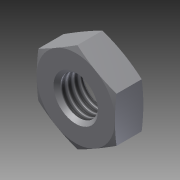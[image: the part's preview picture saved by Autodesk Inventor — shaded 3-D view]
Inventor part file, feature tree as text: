
AUTODESK INVENTOR PART (.ipt)
format: ipt  version: 2012 (Build 160160000, 160)  size: 142,848 bytes
history: native  units: in
note: dims shown in document units (in); Inventor stores cm internally (conversion verified against a paired STEP export)
features: other x70, sketch x3, revolve x2, extrude x1, thread x1
ambient origin geometry x8: Origin, YZ Plane, XZ Plane, XY Plane, X Axis, Y Axis, Z Axis, Center Point
bodies: Solid1 (feature_tree)
feature tree (77):
  sketch  "Sketch_8"  dims[d0=360.0deg d1=0.16in d2=0.0in]
  sketch  "Sketch_10"  dims[d3=360.0deg d4=0.1213in d5=0.0in]
  revolve  "Revolution1"  [1 undecoded]
  extrude  "Extrusion1"  Depth=0.1213in TaperAngle=0.0deg
  revolve  "Revolution2"  [1 undecoded]
  thread  "Thread1"  [1 undecoded]
  other  "NUT_XY"
  other  "NUT_YZ"
  other  "NUT_ZX"
  other  "NUT_X"
  other  "NUT_Y"
  other  "NUT_Z"
  other  "NUT_Center"
  other  "a1_XY"
  other  "a1_YZ"
  other  "a1_ZX"
  other  "a1_X"
  other  "a1_Y"
  other  "a1_Z"
  other  "a1_Center"
  other  "a2_XY"
  other  "a2_YZ"
  other  "a2_ZX"
  other  "a2_X"
  other  "a2_Y"
  other  "a2_Z"
  other  "a2_Center"
  other  "b1_XY"
  other  "b1_YZ"
  other  "b1_ZX"
  other  "b1_X"
  other  "b1_Y"
  other  "b1_Z"
  other  "b1_Center"
  other  "b2_XY"
  other  "b2_YZ"
  other  "b2_ZX"
  other  "b2_X"
  other  "b2_Y"
  other  "b2_Z"
  other  "b2_Center"
  other  "e_XY"
  other  "e_YZ"
  other  "e_ZX"
  other  "e_X"
  other  "e_Y"
  other  "e_Z"
  other  "e_Center"
  other  "th1_XY"
  other  "th1_YZ"
  other  "th1_ZX"
  other  "th1_X"
  other  "th1_Y"
  other  "th1_Z"
  other  "th1_Center"
  other  "th2_XY"
  other  "th2_YZ"
  other  "th2_ZX"
  other  "th2_X"
  other  "th2_Y"
  other  "th2_Z"
  other  "th2_Center"
  other  "ol1_XY"
  other  "ol1_YZ"
  other  "ol1_ZX"
  other  "ol1_X"
  other  "ol1_Y"
  other  "ol1_Z"
  other  "ol1_Center"
  other  "ol2_XY"
  other  "ol2_YZ"
  other  "ol2_ZX"
  other  "ol2_X"
  other  "ol2_Y"
  other  "ol2_Z"
  other  "ol2_Center"
  sketch  "Sketch_11"
note: 3 required parameter values undecoded (feature->parameter linkage not recoverable at this tier; creation-order binding heuristic only, values carry confidence <= 0.55)